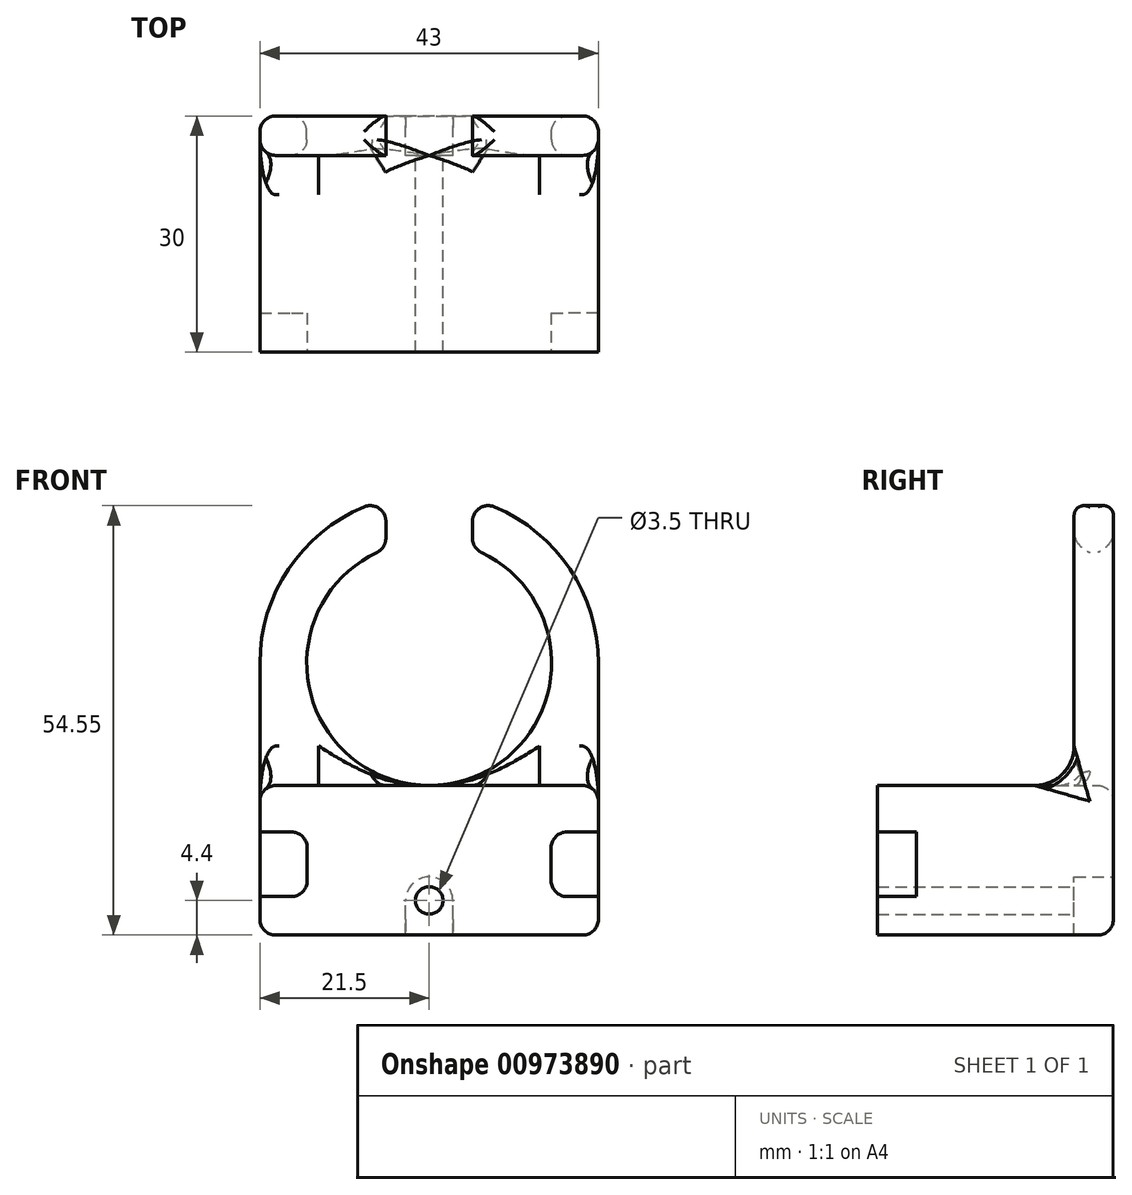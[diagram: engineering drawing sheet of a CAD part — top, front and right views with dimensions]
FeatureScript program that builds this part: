
annotation { "Feature Type Name" : "Feature", "Feature Type Description" : "" }
export const myFeature = defineFeature(function(context is Context, id is Id, definition is map)
    precondition{}
    {
        {
            var Q0;
            Q0=qCreatedBy(makeId("Front.planeOp"),FACE);
            var sketch = newSketch(context, id + "F0", { "sketchPlane" : qUnion([Q0])});
            skLineSegment(sketch, "E0.bottom", {"start": v(0, 0) * mm, "end": v(-43, 0) * mm});
            skLineSegment(sketch, "E0.top", {"start": v(0, 19) * mm, "end": v(-43, 19) * mm, "construction": true});
            skLineSegment(sketch, "E0.left", {"start": v(0, 0) * mm, "end": v(0, 19) * mm});
            skLineSegment(sketch, "E0.right", {"start": v(-43, 0) * mm, "end": v(-43, 19) * mm});
            skArc(sketch, "E1", {"start": v(0, 34.55) * mm, "mid": v(-21.5, 56.05) * mm, "end": v(-43, 34.55) * mm});
            skCircle(sketch, "E2", {"center": v(-21.5, 34.55) * mm, "radius": 15.55 * mm});
            skLineSegment(sketch, "E3", {"start": v(-43, 19) * mm, "end": v(-43, 34.55) * mm});
            skLineSegment(sketch, "E4", {"start": v(0, 19) * mm, "end": v(0, 34.55) * mm});
            skSolve(sketch);
        }
        {
            var Q0;
            Q0 = qSketchRegion(id + "F0", true);
            extrude(context, id + "F1", {"entities" : qUnion([Q0]), "depth" : 5 * mm, "offsetDistance" : 25 * mm});
        }
        {
            var Q0;
            Q0=makeQuery(id+"F1.opExtrude","CAP_FACE",FACE,{"disambiguationData":[OSD([sQuery(id+"F0.wireOp",EDGE,"E0.bottom"),sQuery(id+"F0.wireOp",EDGE,"E0.left"),sQuery(id+"F0.wireOp",EDGE,"E0.right"),sQuery(id+"F0.wireOp",EDGE,"E1"),sQuery(id+"F0.wireOp",EDGE,"E2"),sQuery(id+"F0.wireOp",EDGE,"E3"),sQuery(id+"F0.wireOp",EDGE,"E4")])],"isStart":false});
            var sketch = newSketch(context, id + "F2", { "sketchPlane" : qUnion([Q0])});
            skLineSegment(sketch, "E5", {"start": v(-21.5, 34.55) * mm, "end": v(-21.5, 59.55) * mm, "construction": true});
            skLineSegment(sketch, "E6.bottom", {"start": v(-27, 59.55) * mm, "end": v(-16, 59.55) * mm});
            skLineSegment(sketch, "E6.top", {"start": v(-27, 47.55) * mm, "end": v(-16, 47.55) * mm});
            skLineSegment(sketch, "E6.left", {"start": v(-27, 59.55) * mm, "end": v(-27, 47.55) * mm});
            skLineSegment(sketch, "E6.right", {"start": v(-16, 59.55) * mm, "end": v(-16, 47.55) * mm});
            skSolve(sketch);
        }
        {
            var Q0;
            Q0 = qSketchRegion(id + "F2", true);
            var Q1;
            Q1=makeQuery(id+"F1.opExtrude","CAP_FACE",FACE,{"disambiguationData":[OSD([sQuery(id+"F0.wireOp",EDGE,"E0.bottom"),sQuery(id+"F0.wireOp",EDGE,"E0.left"),sQuery(id+"F0.wireOp",EDGE,"E0.right"),sQuery(id+"F0.wireOp",EDGE,"E1"),sQuery(id+"F0.wireOp",EDGE,"E2"),sQuery(id+"F0.wireOp",EDGE,"E3"),sQuery(id+"F0.wireOp",EDGE,"E4")])],"isStart":true});
            extrude(context, id + "F3", {"entities" : qUnion([Q0]), "operationType" : NewBodyOperationType.REMOVE, "endBound" : BoundingType.UP_TO_SURFACE, "oppositeDirection" : true, "depth" : 25 * mm, "endBoundEntityFace" : qUnion([Q1]), "offsetDistance" : 25 * mm});
        }
        {
            var Q0;
            Q0=makeQuery(id+"F1.opExtrude","CAP_FACE",FACE,{"disambiguationData":[OSD([sQuery(id+"F0.wireOp",EDGE,"E0.bottom"),sQuery(id+"F0.wireOp",EDGE,"E0.left"),sQuery(id+"F0.wireOp",EDGE,"E0.right"),sQuery(id+"F0.wireOp",EDGE,"E1"),sQuery(id+"F0.wireOp",EDGE,"E2"),sQuery(id+"F0.wireOp",EDGE,"E3"),sQuery(id+"F0.wireOp",EDGE,"E4")])],"isStart":false});
            var sketch = newSketch(context, id + "F4", { "sketchPlane" : qUnion([Q0])});
            skLineSegment(sketch, "E7.bottom", {"start": v(-43, 0) * mm, "end": v(0, 0) * mm});
            skLineSegment(sketch, "E7.top", {"start": v(-43, 19) * mm, "end": v(0, 19) * mm});
            skLineSegment(sketch, "E7.left", {"start": v(-43, 0) * mm, "end": v(-43, 19) * mm});
            skLineSegment(sketch, "E7.right", {"start": v(0, 0) * mm, "end": v(0, 19) * mm});
            skSolve(sketch);
        }
        {
            var Q0;
            Q0 = qSketchRegion(id + "F4", true);
            extrude(context, id + "F5", {"entities" : qUnion([Q0]), "operationType" : NewBodyOperationType.ADD, "depth" : 25 * mm, "offsetDistance" : 25 * mm});
        }
        {
            var Q0;
            Q0=makeQuery(id+"F5.opExtrude","CAP_FACE",FACE,{"disambiguationData":[OSD([sQuery(id+"F4.wireOp",EDGE,"E7.bottom"),sQuery(id+"F4.wireOp",EDGE,"E7.top"),sQuery(id+"F4.wireOp",EDGE,"E7.left"),sQuery(id+"F4.wireOp",EDGE,"E7.right")])],"isStart":false});
            var sketch = newSketch(context, id + "F6", { "sketchPlane" : qUnion([Q0])});
            skLineSegment(sketch, "E8.bottom", {"start": v(-43, 13.1) * mm, "end": v(-37, 13.1) * mm});
            skLineSegment(sketch, "E8.top", {"start": v(-43, 4.9) * mm, "end": v(-37, 4.9) * mm});
            skLineSegment(sketch, "E8.left", {"start": v(-43, 13.1) * mm, "end": v(-43, 4.9) * mm});
            skLineSegment(sketch, "E8.right", {"start": v(-37, 13.1) * mm, "end": v(-37, 4.9) * mm});
            skLineSegment(sketch, "E9.bottom", {"start": v(0, 13.1) * mm, "end": v(-6, 13.1) * mm});
            skLineSegment(sketch, "E9.top", {"start": v(0, 4.9) * mm, "end": v(-6, 4.9) * mm});
            skLineSegment(sketch, "E9.left", {"start": v(0, 13.1) * mm, "end": v(0, 4.9) * mm});
            skLineSegment(sketch, "E9.right", {"start": v(-6, 13.1) * mm, "end": v(-6, 4.9) * mm});
            skSolve(sketch);
        }
        {
            var Q0;
            Q0 = qSketchRegion(id + "F6", true);
            extrude(context, id + "F7", {"entities" : qUnion([Q0]), "operationType" : NewBodyOperationType.REMOVE, "oppositeDirection" : true, "depth" : 5 * mm, "offsetDistance" : 25 * mm});
        }
        {
            var Q0;
            Q0=makeQuery(id+"F0.imprint","IMPRINT",FACE,{"disambiguationData":[TD([[makeQuery(id+"F0.imprint","IMPRINT",EDGE,{"derivedFrom":sQuery(id+"F0.wireOp",EDGE,"E0.bottom")}),-1.0]])]});
            var sketch = newSketch(context, id + "F8", { "sketchPlane" : qUnion([Q0])});
            skLineSegment(sketch, "E10", {"start": v(-21.5, 0) * mm, "end": v(-21.5, 4.4) * mm});
            skArc(sketch, "E11.0.startCap", {"start": v(-18.5, 0) * mm, "mid": v(-21.5, -3) * mm, "end": v(-24.5, 0) * mm});
            skArc(sketch, "E11.0.endCap", {"start": v(-24.5, 4.4) * mm, "mid": v(-21.5, 7.4) * mm, "end": v(-18.5, 4.4) * mm});
            skLineSegment(sketch, "E11.0.left", {"start": v(-24.5, 0) * mm, "end": v(-24.5, 4.4) * mm});
            skLineSegment(sketch, "E11.0.right", {"start": v(-18.5, 0) * mm, "end": v(-18.5, 4.4) * mm});
            skSolve(sketch);
        }
        {
            var Q0;
            Q0 = qSketchRegion(id + "F8", true);
            extrude(context, id + "F9", {"entities" : qUnion([Q0]), "operationType" : NewBodyOperationType.REMOVE, "depth" : 5 * mm, "offsetDistance" : 25 * mm});
        }
        {
            var Q0;
            Q0=makeQuery(id+"F5.boolean.opBoolean","MERGE",EDGE,{"derivedFrom":[makeQuery(id+"F1.opExtrude","SWEPT_EDGE",EDGE,{"disambiguationData":[OSD([sQuery(id+"F0.wireOp",EDGE,"E0.bottom"),sQuery(id+"F0.wireOp",EDGE,"E0.right")])]}),makeQuery(id+"F5.opExtrude","SWEPT_EDGE",EDGE,{"disambiguationData":[OSD([sQuery(id+"F4.wireOp",EDGE,"E7.bottom"),sQuery(id+"F4.wireOp",EDGE,"E7.left")])]})]});
            var Q1;
            Q1=makeQuery(id+"F1.opExtrude","CAP_EDGE",EDGE,{"disambiguationData":[OSD([sQuery(id+"F0.wireOp",EDGE,"E2")])],"isStart":false});
            var Q2;
            Q2=makeQuery(id+"F1.opExtrude","CAP_EDGE",EDGE,{"disambiguationData":[OSD([sQuery(id+"F0.wireOp",EDGE,"E2")])],"isStart":true});
            var Q3;
            {var subQ1=sQuery(id+"F0.wireOp",EDGE,"E1");Q3=makeQuery(id+"F3.boolean.opBoolean","SPLIT",EDGE,{"disambiguationData":[TD([makeQuery(id+"F3.opExtrude","SWEPT_FACE",FACE,{"disambiguationData":[OSD([sQuery(id+"F2.wireOp",EDGE,"E6.left")])]})])],"derivedFrom":makeQuery(id+"F1.opExtrude","CAP_EDGE",EDGE,{"disambiguationData":[OSD([subQ1])],"isStart":false})});}
            var Q4;
            {var subQ1=sQuery(id+"F0.wireOp",EDGE,"E1");Q4=makeQuery(id+"F3.boolean.opBoolean","SPLIT",EDGE,{"disambiguationData":[TD([makeQuery(id+"F3.opExtrude","SWEPT_FACE",FACE,{"disambiguationData":[OSD([sQuery(id+"F2.wireOp",EDGE,"E6.left")])]})])],"derivedFrom":makeQuery(id+"F1.opExtrude","CAP_EDGE",EDGE,{"disambiguationData":[OSD([subQ1])],"isStart":true})});}
            var Q5;
            Q5=makeQuery(id+"F1.opExtrude","CAP_EDGE",EDGE,{"disambiguationData":[OSD([sQuery(id+"F0.wireOp",EDGE,"E0.left"),sQuery(id+"F0.wireOp",EDGE,"E4")])],"isStart":true});
            var Q6;
            Q6=makeQuery(id+"F5.boolean.opBoolean","MERGE",EDGE,{"derivedFrom":[makeQuery(id+"F1.opExtrude","SWEPT_EDGE",EDGE,{"disambiguationData":[OSD([sQuery(id+"F0.wireOp",EDGE,"E0.bottom"),sQuery(id+"F0.wireOp",EDGE,"E0.left")])]}),makeQuery(id+"F5.opExtrude","SWEPT_EDGE",EDGE,{"disambiguationData":[OSD([sQuery(id+"F4.wireOp",EDGE,"E7.bottom"),sQuery(id+"F4.wireOp",EDGE,"E7.right")])]})]});
            var Q7;
            Q7=makeQuery(id+"F1.opExtrude","CAP_EDGE",EDGE,{"disambiguationData":[OSD([sQuery(id+"F0.wireOp",EDGE,"E0.left"),sQuery(id+"F0.wireOp",EDGE,"E4")])],"isStart":false});
            var Q8;
            Q8=makeQuery(id+"F5.opExtrude","SWEPT_EDGE",EDGE,{"disambiguationData":[OSD([sQuery(id+"F0.wireOp",EDGE,"E0.left"),sQuery(id+"F0.wireOp",EDGE,"E4"),sQuery(id+"F4.wireOp",EDGE,"E7.top"),sQuery(id+"F4.wireOp",EDGE,"E7.right")])]});
            var Q9;
            Q9=makeQuery(id+"F5.opExtrude","SWEPT_EDGE",EDGE,{"disambiguationData":[OSD([sQuery(id+"F0.wireOp",EDGE,"E0.right"),sQuery(id+"F0.wireOp",EDGE,"E3"),sQuery(id+"F4.wireOp",EDGE,"E7.top"),sQuery(id+"F4.wireOp",EDGE,"E7.left")])]});
            var Q10;
            Q10=makeQuery(id+"F3.boolean.opBoolean","COPY",EDGE,{"derivedFrom":makeQuery(id+"F3.opExtrude","CAP_EDGE",EDGE,{"disambiguationData":[OSD([sQuery(id+"F2.wireOp",EDGE,"E6.right")])],"isStart":true})});
            var Q11;
            Q11=makeQuery(id+"F3.boolean.opBoolean","COPY",EDGE,{"derivedFrom":makeQuery(id+"F3.opExtrude","CAP_EDGE",EDGE,{"disambiguationData":[OSD([sQuery(id+"F2.wireOp",EDGE,"E6.right")])],"isStart":false})});
            var Q12;
            Q12=makeQuery(id+"F3.boolean.opBoolean","INTERSECT",EDGE,{"derivedFrom":[makeQuery(id+"F1.opExtrude","SWEPT_FACE",FACE,{"disambiguationData":[OSD([sQuery(id+"F0.wireOp",EDGE,"E1")])]}),makeQuery(id+"F3.opExtrude","SWEPT_FACE",FACE,{"disambiguationData":[OSD([sQuery(id+"F2.wireOp",EDGE,"E6.right")])]})]});
            var Q13;
            Q13=makeQuery(id+"F3.boolean.opBoolean","INTERSECT",EDGE,{"derivedFrom":[makeQuery(id+"F1.opExtrude","SWEPT_FACE",FACE,{"disambiguationData":[OSD([sQuery(id+"F0.wireOp",EDGE,"E2")])]}),makeQuery(id+"F3.opExtrude","SWEPT_FACE",FACE,{"disambiguationData":[OSD([sQuery(id+"F2.wireOp",EDGE,"E6.right")])]})]});
            var Q14;
            Q14=makeQuery(id+"F3.boolean.opBoolean","INTERSECT",EDGE,{"derivedFrom":[makeQuery(id+"F1.opExtrude","SWEPT_FACE",FACE,{"disambiguationData":[OSD([sQuery(id+"F0.wireOp",EDGE,"E2")])]}),makeQuery(id+"F3.opExtrude","SWEPT_FACE",FACE,{"disambiguationData":[OSD([sQuery(id+"F2.wireOp",EDGE,"E6.left")])]})]});
            var Q15;
            Q15=makeQuery(id+"F3.boolean.opBoolean","COPY",EDGE,{"derivedFrom":makeQuery(id+"F3.opExtrude","CAP_EDGE",EDGE,{"disambiguationData":[OSD([sQuery(id+"F2.wireOp",EDGE,"E6.left")])],"isStart":false})});
            var Q16;
            Q16=makeQuery(id+"F3.boolean.opBoolean","COPY",EDGE,{"derivedFrom":makeQuery(id+"F3.opExtrude","CAP_EDGE",EDGE,{"disambiguationData":[OSD([sQuery(id+"F2.wireOp",EDGE,"E6.left")])],"isStart":true})});
            var Q17;
            Q17=makeQuery(id+"F3.boolean.opBoolean","INTERSECT",EDGE,{"derivedFrom":[makeQuery(id+"F1.opExtrude","SWEPT_FACE",FACE,{"disambiguationData":[OSD([sQuery(id+"F0.wireOp",EDGE,"E1")])]}),makeQuery(id+"F3.opExtrude","SWEPT_FACE",FACE,{"disambiguationData":[OSD([sQuery(id+"F2.wireOp",EDGE,"E6.left")])]})]});
            var Q18;
            Q18=makeQuery(id+"F1.opExtrude","CAP_EDGE",EDGE,{"disambiguationData":[OSD([sQuery(id+"F0.wireOp",EDGE,"E0.bottom")])],"isStart":true});
            var Q19;
            Q19=makeQuery(id+"F7.boolean.opBoolean","COPY",EDGE,{"derivedFrom":makeQuery(id+"F7.opExtrude","SWEPT_EDGE",EDGE,{"disambiguationData":[OSD([sQuery(id+"F6.wireOp",EDGE,"E8.bottom"),sQuery(id+"F6.wireOp",EDGE,"E8.right")])]})});
            var Q20;
            Q20=makeQuery(id+"F7.boolean.opBoolean","COPY",EDGE,{"derivedFrom":makeQuery(id+"F7.opExtrude","SWEPT_EDGE",EDGE,{"disambiguationData":[OSD([sQuery(id+"F6.wireOp",EDGE,"E8.top"),sQuery(id+"F6.wireOp",EDGE,"E8.right")])]})});
            var Q21;
            Q21=makeQuery(id+"F7.boolean.opBoolean","COPY",EDGE,{"derivedFrom":makeQuery(id+"F7.opExtrude","SWEPT_EDGE",EDGE,{"disambiguationData":[OSD([sQuery(id+"F6.wireOp",EDGE,"E9.bottom"),sQuery(id+"F6.wireOp",EDGE,"E9.right")])]})});
            var Q22;
            Q22=makeQuery(id+"F7.boolean.opBoolean","COPY",EDGE,{"derivedFrom":makeQuery(id+"F7.opExtrude","SWEPT_EDGE",EDGE,{"disambiguationData":[OSD([sQuery(id+"F6.wireOp",EDGE,"E9.top"),sQuery(id+"F6.wireOp",EDGE,"E9.right")])]})});
            var Q23;
            Q23=makeQuery(id+"F9.boolean.opBoolean","COPY",EDGE,{"derivedFrom":makeQuery(id+"F9.opExtrude","CAP_EDGE",EDGE,{"disambiguationData":[OSD([sQuery(id+"F8.wireOp",EDGE,"E11.0.left")])],"isStart":true})});
            fillet(context, id + "F10", {"entities" : qUnion([Q0, Q1, Q2, Q3, Q4, Q5, Q6, Q7, Q8, Q9, Q10, Q11, Q12, Q13, Q14, Q15, Q16, Q17, Q18, Q19, Q20, Q21, Q22, Q23]), "radius" : 2 * mm, "tangentPropagation" : true, "allowEdgeOverflow" : false});
        }
        {
            var Q0;
            Q0=makeQuery(id+"F5.opExtrude","CAP_EDGE",EDGE,{"disambiguationData":[OSD([sQuery(id+"F4.wireOp",EDGE,"E7.top")])],"isStart":true});
            fillet(context, id + "F11", {"entities" : qUnion([Q0]), "radius" : 5 * mm, "tangentPropagation" : true, "allowEdgeOverflow" : false});
        }
        {
            var Q0;
            Q0=makeQuery(id+"F0.imprint","IMPRINT",FACE,{"disambiguationData":[TD([[makeQuery(id+"F0.imprint","IMPRINT",EDGE,{"derivedFrom":sQuery(id+"F0.wireOp",EDGE,"E0.bottom")}),-1.0]])]});
            var sketch = newSketch(context, id + "F12", { "sketchPlane" : qUnion([Q0])});
            skCircle(sketch, "E12", {"center": v(-21.5, 4.4) * mm, "radius": 1.75 * mm});
            skSolve(sketch);
        }
        {
            var Q0;
            Q0 = qSketchRegion(id + "F12", true);
            var Q1;
            Q1=makeQuery(id+"F5.opExtrude","CAP_FACE",FACE,{"disambiguationData":[OSD([sQuery(id+"F4.wireOp",EDGE,"E7.bottom"),sQuery(id+"F4.wireOp",EDGE,"E7.top"),sQuery(id+"F4.wireOp",EDGE,"E7.left"),sQuery(id+"F4.wireOp",EDGE,"E7.right")])],"isStart":false});
            extrude(context, id + "F13", {"entities" : qUnion([Q0]), "operationType" : NewBodyOperationType.REMOVE, "endBound" : BoundingType.UP_TO_SURFACE, "depth" : 25 * mm, "endBoundEntityFace" : qUnion([Q1]), "offsetDistance" : 25 * mm});
        }
    });
